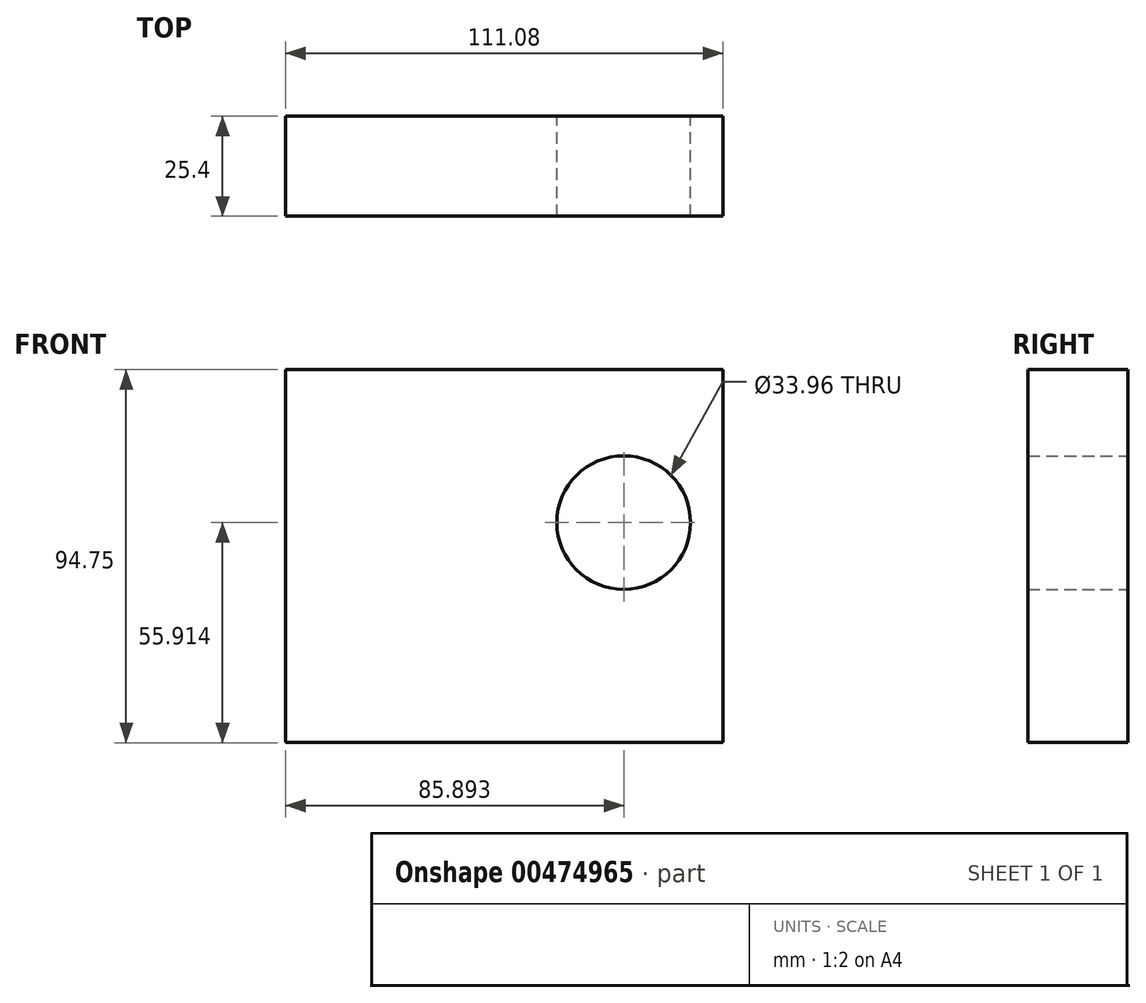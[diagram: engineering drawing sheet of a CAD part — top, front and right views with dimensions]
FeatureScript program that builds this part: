
annotation { "Feature Type Name" : "Feature", "Feature Type Description" : "" }
export const myFeature = defineFeature(function(context is Context, id is Id, definition is map)
    precondition{}
    {
        {
            var Q0;
            Q0=qCreatedBy(makeId("Front.planeOp"),FACE);
            var sketch = newSketch(context, id + "F0", { "sketchPlane" : qUnion([Q0])});
            skLineSegment(sketch, "E0.bottom", {"start": v(-44.4, 55.42) * mm, "end": v(66.67, 55.42) * mm});
            skLineSegment(sketch, "E0.top", {"start": v(-44.4, -39.33) * mm, "end": v(66.67, -39.33) * mm});
            skLineSegment(sketch, "E0.left", {"start": v(-44.4, 55.42) * mm, "end": v(-44.4, -39.33) * mm});
            skLineSegment(sketch, "E0.right", {"start": v(66.67, 55.42) * mm, "end": v(66.67, -39.33) * mm});
            skCircle(sketch, "E1", {"center": v(41.48, 16.58) * mm, "radius": 16.98 * mm});
            skSolve(sketch);
        }
        {
            var Q0;
            Q0 = qSketchRegion(id + "F0", true);
            extrude(context, id + "F1", {"entities" : qUnion([Q0]), "depth" : 25.4 * mm});
        }
    });
